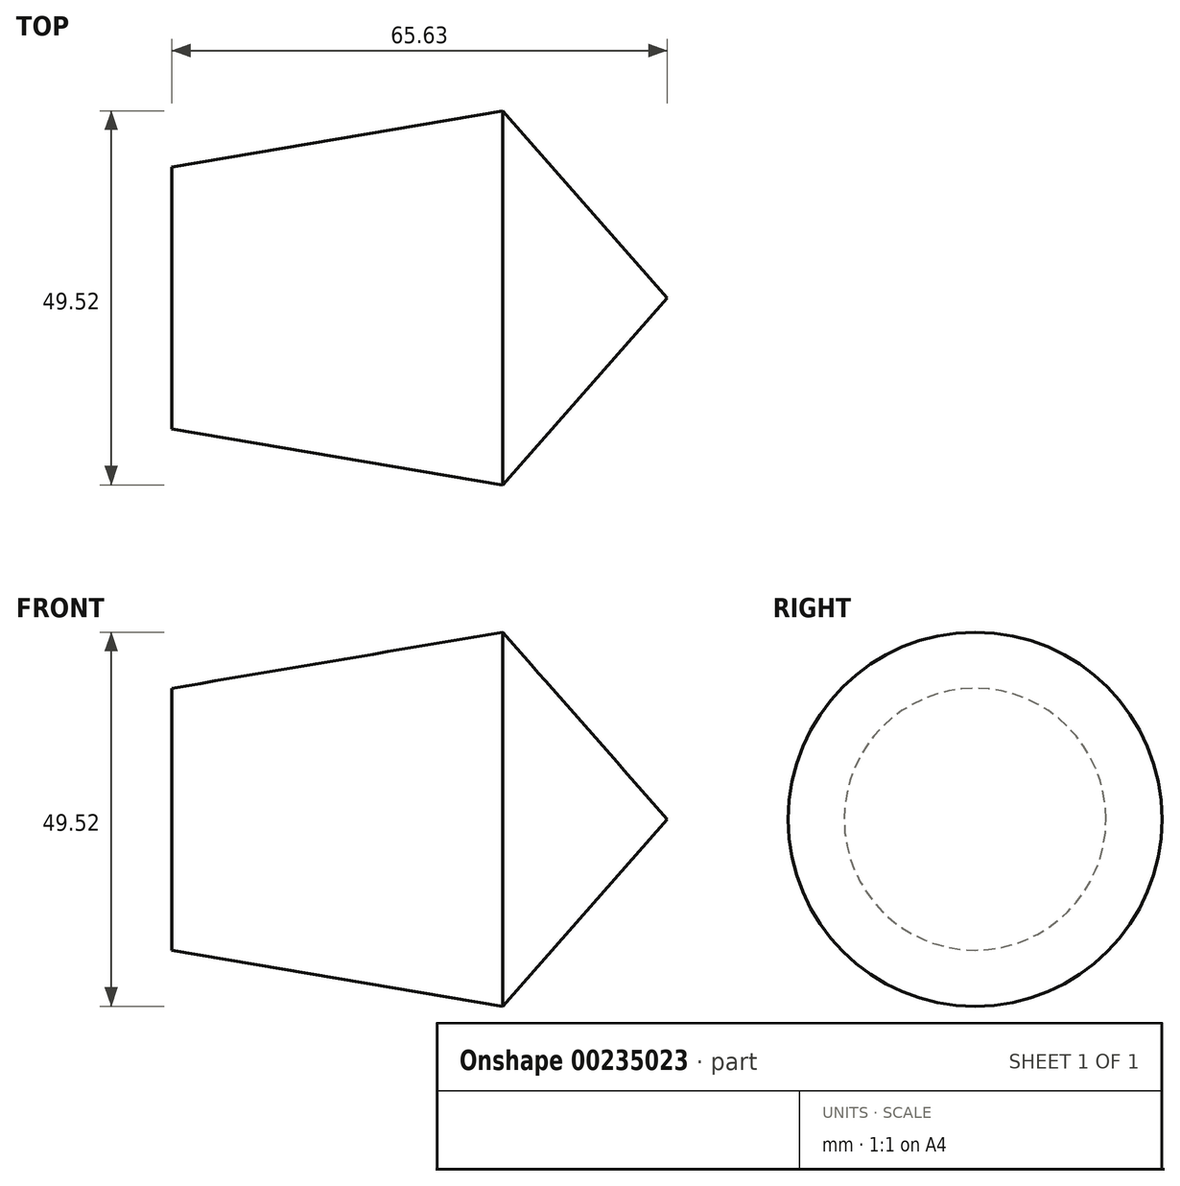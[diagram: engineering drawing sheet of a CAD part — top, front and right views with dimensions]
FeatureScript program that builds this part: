
annotation { "Feature Type Name" : "Feature", "Feature Type Description" : "" }
export const myFeature = defineFeature(function(context is Context, id is Id, definition is map)
    precondition{}
    {
        {
            var Q0;
            Q0=qCreatedBy(makeId("Top.planeOp"),FACE);
            var sketch = newSketch(context, id + "F0", { "sketchPlane" : qUnion([Q0])});
            skLineSegment(sketch, "E0", {"start": v(0, 0) * mm, "end": v(0, 17.33) * mm});
            skLineSegment(sketch, "E1", {"start": v(0, 17.33) * mm, "end": v(43.83, 24.76) * mm});
            skLineSegment(sketch, "E2", {"start": v(43.83, 24.76) * mm, "end": v(65.63, 0) * mm});
            skLineSegment(sketch, "E3", {"start": v(65.63, 0) * mm, "end": v(0, 0) * mm});
            skSolve(sketch);
        }
        {
            var Q0;
            Q0=sQuery(id+"F0.wireOp",EDGE,"E2");
            var Q1;
            Q1=sQuery(id+"F0.wireOp",EDGE,"E1");
            var Q2;
            Q2=sQuery(id+"F0.wireOp",EDGE,"E0");
            var Q3;
            Q3=sQuery(id+"F0.wireOp",EDGE,"E3");
            revolve(context, id + "F1", {"bodyType" : ToolBodyType.SURFACE, "surfaceEntities" : qUnion([Q0, Q1, Q2]), "axis" : qUnion([Q3]), "revolveType" : RevolveType.ONE_DIRECTION, "angle" : 360 * degree});
        }
    });
